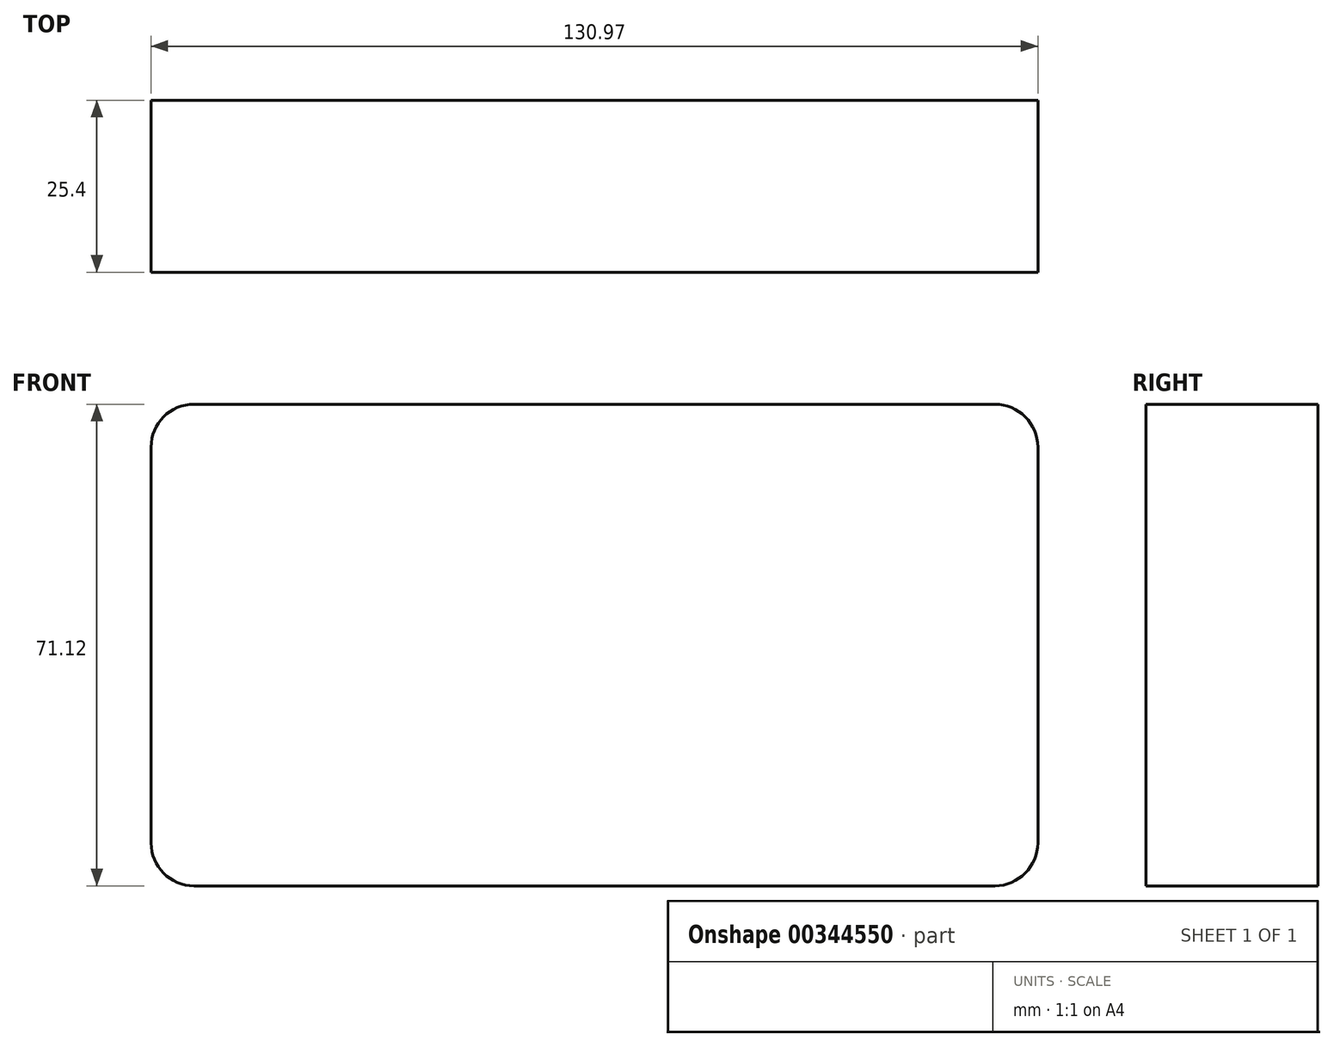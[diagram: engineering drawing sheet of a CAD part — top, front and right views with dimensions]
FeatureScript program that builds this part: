
annotation { "Feature Type Name" : "Feature", "Feature Type Description" : "" }
export const myFeature = defineFeature(function(context is Context, id is Id, definition is map)
    precondition{}
    {
        {
            var Q0;
            Q0=qCreatedBy(makeId("Front.planeOp"),FACE);
            var sketch = newSketch(context, id + "F0", { "sketchPlane" : qUnion([Q0])});
            skLineSegment(sketch, "E0.bottom", {"start": v(-58.5, 34.43) * mm, "end": v(59.76, 34.43) * mm});
            skLineSegment(sketch, "E0.top", {"start": v(-58.5, -36.69) * mm, "end": v(59.76, -36.69) * mm});
            skLineSegment(sketch, "E0.left", {"start": v(-64.86, 28.08) * mm, "end": v(-64.86, -30.34) * mm});
            skLineSegment(sketch, "E0.right", {"start": v(66.11, 28.08) * mm, "end": v(66.11, -30.34) * mm});
            skPoint(sketch, "E1.visualSharp", {"position": v(-64.86, 34.43) * mm});
            skArc(sketch, "E1.filletArc", {"start": v(-58.5, 34.43) * mm, "mid": v(-63, 32.57) * mm, "end": v(-64.86, 28.08) * mm});
            skPoint(sketch, "E2.visualSharp", {"position": v(66.11, 34.43) * mm});
            skArc(sketch, "E2.filletArc", {"start": v(66.11, 28.08) * mm, "mid": v(64.25, 32.57) * mm, "end": v(59.76, 34.43) * mm});
            skPoint(sketch, "E3.visualSharp", {"position": v(66.11, -36.69) * mm});
            skArc(sketch, "E3.filletArc", {"start": v(59.76, -36.69) * mm, "mid": v(64.25, -34.83) * mm, "end": v(66.11, -30.34) * mm});
            skPoint(sketch, "E4.visualSharp", {"position": v(-64.86, -36.69) * mm});
            skArc(sketch, "E4.filletArc", {"start": v(-64.86, -30.34) * mm, "mid": v(-63, -34.83) * mm, "end": v(-58.5, -36.69) * mm});
            skSolve(sketch);
        }
        {
            var Q0;
            Q0=makeQuery(id+"F0.imprint","IMPRINT",FACE,{"disambiguationData":[TD([[makeQuery(id+"F0.imprint","IMPRINT",EDGE,{"derivedFrom":sQuery(id+"F0.wireOp",EDGE,"E0.bottom")}),-1.0]])]});
            extrude(context, id + "F1", {"entities" : qUnion([Q0]), "depth" : 25.4 * mm});
        }
    });
